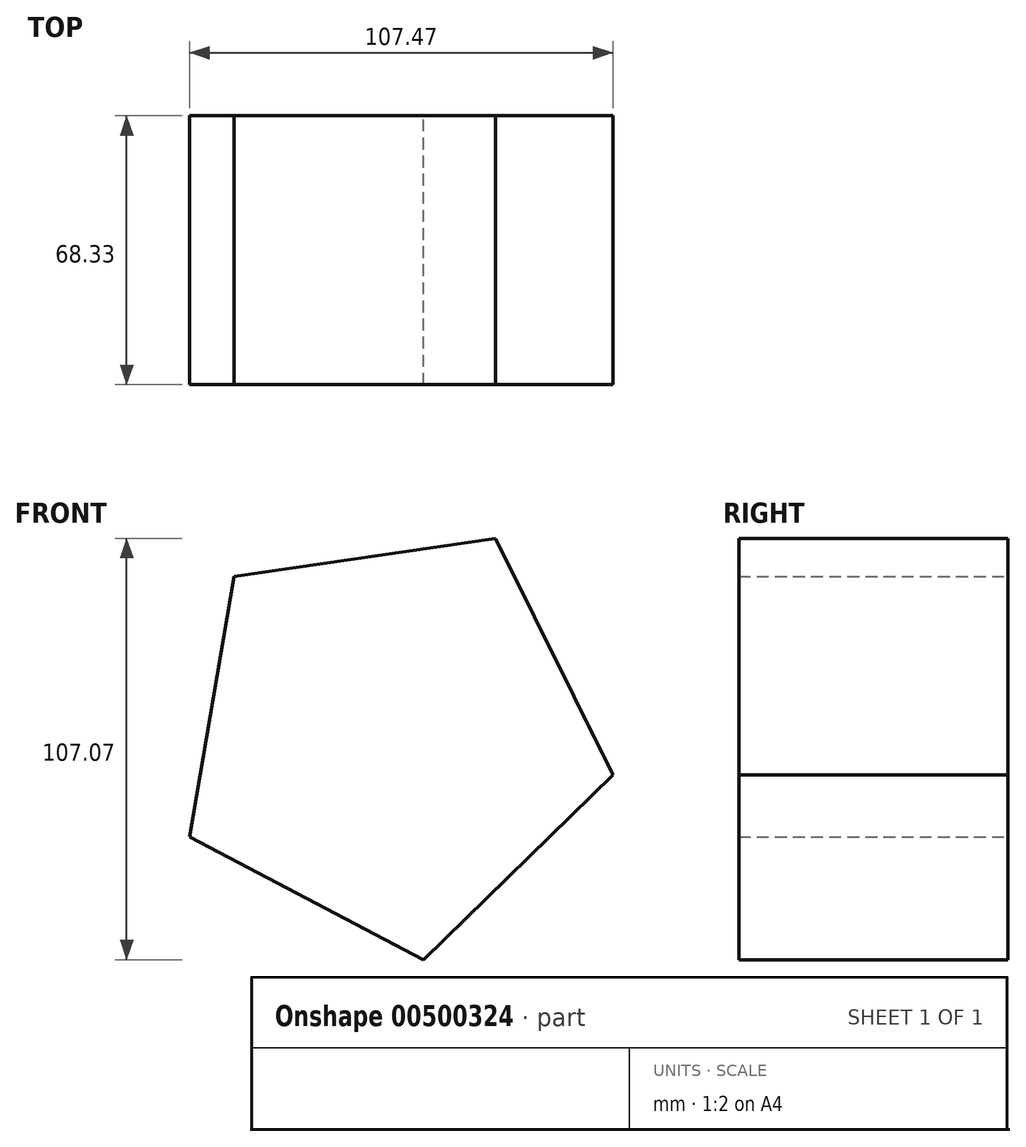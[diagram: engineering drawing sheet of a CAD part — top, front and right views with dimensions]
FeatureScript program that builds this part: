
annotation { "Feature Type Name" : "Feature", "Feature Type Description" : "" }
export const myFeature = defineFeature(function(context is Context, id is Id, definition is map)
    precondition{}
    {
        {
            var Q0;
            Q0=qCreatedBy(makeId("Front.planeOp"),FACE);
            var sketch = newSketch(context, id + "F0", { "sketchPlane" : qUnion([Q0])});
            skCircle(sketch, "E0.cCircle", {"center": v(0, 0) * mm, "radius": 57.1 * mm, "construction": true});
            skLineSegment(sketch, "E0.0", {"start": v(26.52, 50.57) * mm, "end": v(56.3, -9.6) * mm});
            skLineSegment(sketch, "E0.1", {"start": v(56.3, -9.6) * mm, "end": v(8.27, -56.5) * mm});
            skLineSegment(sketch, "E0.2", {"start": v(8.27, -56.5) * mm, "end": v(-51.18, -25.32) * mm});
            skLineSegment(sketch, "E0.3", {"start": v(-51.18, -25.32) * mm, "end": v(-39.9, 40.85) * mm});
            skLineSegment(sketch, "E0.4", {"start": v(-39.9, 40.85) * mm, "end": v(26.52, 50.57) * mm});
            skSolve(sketch);
        }
        {
            var Q0;
            Q0 = qSketchRegion(id + "F0", true);
            extrude(context, id + "F1", {"entities" : qUnion([Q0]), "depth" : 68.33 * mm});
        }
    });
